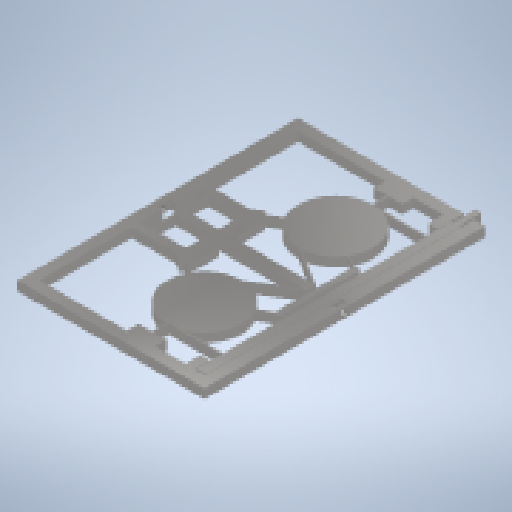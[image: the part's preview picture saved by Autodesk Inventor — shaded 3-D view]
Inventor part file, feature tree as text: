
AUTODESK INVENTOR PART (.ipt)
format: ipt  version: 2023 (Build 270158000, 158)  size: 535,552 bytes
history: native  units: mm
features: extrude x6, sketch x6, other x1
ambient origin geometry x8: Origin, YZ Plane, XZ Plane, XY Plane, X Axis, Y Axis, Z Axis, Center Point
bodies: Solid1 (feature_tree)
feature tree (13):
  other  "<userpath>\OneDrive\ClawdDrive\Objet3D\IminaProbe\Settings.xlsx"
  extrude  "Extrusion1"  Depth=100.0mm
  extrude  "Extrusion6"  TaperAngle=0.0deg  [1 undecoded]
  extrude  "Extrusion7"  Depth=1.0mm
  extrude  "Extrusion9"  Depth=1.0mm
  extrude  "Extrusion10"  Depth=50.0mm
  extrude  "Extrusion11"  Depth=6.0mm
  sketch  "Sketch1"  dims[d0=150.0mm d1=100.0mm]
  sketch  "Sketch6"  dims[d2=5.0mm d3=0.0mm]
  sketch  "Sketch7"  dims[d14=1.0mm d16=1.0mm]
  sketch  "Sketch9"  dims[d19=1.0mm d23=52.849025mm d24=57.849025mm]
  sketch  "Sketch10"  dims[d25=67.849025mm]
  sketch  "Sketch11"  dims[d31=45.0deg d32=45.0deg d33=45.0deg d34=45.0deg d40=45.0deg d45=45.0deg d46=45.0deg d47=45.0deg d80=50.0mm d81=50.0mm d89=6.0mm d90=6.0mm d91=6.0mm d92=6.0mm d93=5.0mm d94=136.0mm d95=1.0mm d96=8.0mm d97=5.0mm d98=5.5mm d100=5.0mm d101=5.5mm d103=3.0mm d104=20.0mm d105=1.0mm d106=0.25mm d112=40.0mm d113=40.0mm d116=1.0mm d117=1.0mm d118=1.0mm d119=1.0mm d120=11.34464mm d121=11.34464mm d124=25.0mm d125=30.0mm d126=5.0mm d127=5.0mm d128=40.0mm d129=55.0mm d130=20.0mm d131=20.0mm d132=20.0mm d133=20.0mm d134=1.0mm d135=1.0mm d138=10.12291mm d139=10.12291mm d140=10.12291mm d141=10.12291mm d142=15.0mm d145=8.0mm d150=1.0mm d151=1.0mm d152=5.0mm d153=2.0mm d154=2.0mm d155=5.0mm d156=5.0mm d157=15.0mm d158=15.0mm d159=40.0mm d160=40.0mm d161=0.0mm d162=5.0mm d165=30.0mm d167=360.0deg d169=30.0deg d171=2.0mm d172=5.0mm d173=3.0mm d175=1.5mm d176=1.0mm d177=0.5mm d178=0.5mm d179=28.0mm d180=0.0mm d181=28.0mm d182=30.0mm d184=360.0deg d186=30.0deg d187=3.0mm d188=1.5mm d189=1.0mm d190=0.5mm d192=0.0mm d193=0.0mm d194=5.0mm d195=2.5mm d196=0.5mm d199=0.5mm d200=8.0mm d201=8.0mm d202=8.0mm d203=8.0mm d204=0.5mm d205=0.5mm d206=5.0mm d207=2.5mm d209=5.0mm d211=2.5mm d212=0.5mm d213=0.5mm d214=8.0mm d215=20.0mm d216=20.0mm d217=20.0mm d218=20.0mm d219=5.0mm d220=0.5mm d221=0.5mm d222=2.5mm d223=5.0mm d224=5.0mm d225=5.0mm d226=5.0mm d227=1.0mm d228=1.0mm d229=8.0mm d230=1.0mm d231=1.0mm d233=2.0mm d234=3.0mm d235=3.0mm d237=3.0mm d238=3.0mm d239=10.0mm d240=0.0mm d241=6.5mm d242=6.5mm d244=3.25mm d245=3.25mm d246=6.5mm d247=6.5mm d248=3.25mm d249=3.25mm d250=6.5mm d251=0.75mm d252=0.0mm d253=5.0mm d254=5.0mm d255=0.0mm d259=10.0mm d265=3.0mm d266=6.5mm d267=6.0mm d268=1.0mm d269=150.0mm d270=71.75mm d271=10.0mm d272=0.0mm d273=75.0mm d274=3.5mm d275=2.5mm d276=5.0mm d277=12.0mm d278=0.0mm d279=5.0mm d280=2.5mm d281=3.5mm d282=75.0mm d283=8.0mm d284=0.0mm d285=0.5mm d286=0.5mm d287=0.0mm]
note: 1 required parameter value undecoded (feature->parameter linkage not recoverable at this tier; creation-order binding heuristic only, values carry confidence <= 0.55)
